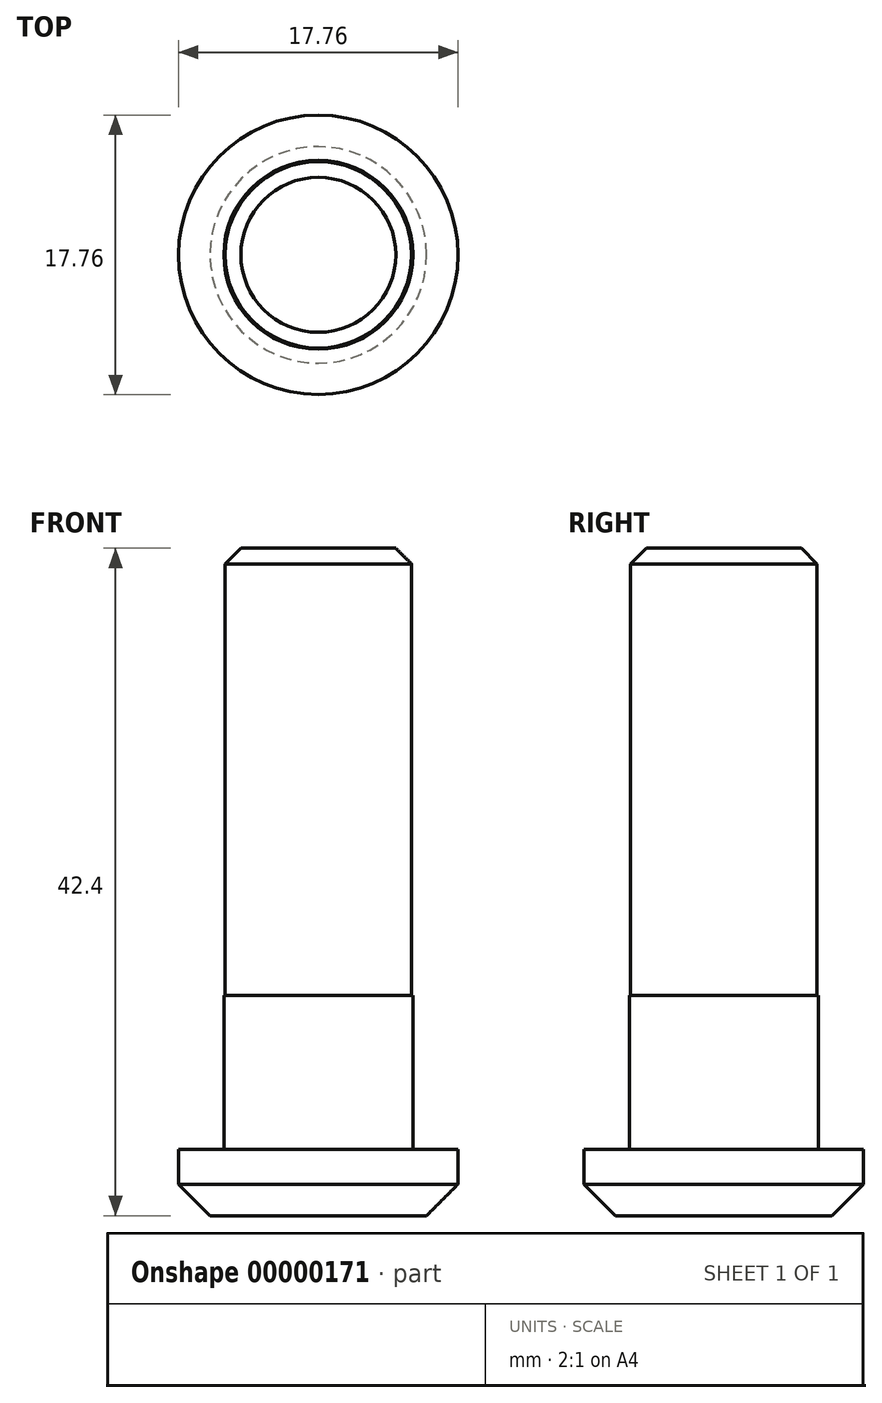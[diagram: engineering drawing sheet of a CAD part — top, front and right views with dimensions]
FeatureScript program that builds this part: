
annotation { "Feature Type Name" : "Feature", "Feature Type Description" : "" }
export const myFeature = defineFeature(function(context is Context, id is Id, definition is map)
    precondition{}
    {
        {
            var Q0;
            Q0=qCreatedBy(makeId("Top.planeOp"),FACE);
            var sketch = newSketch(context, id + "F0", { "sketchPlane" : qUnion([Q0])});
            skCircle(sketch, "E0", {"center": v(0, 0) * mm, "radius": 8.88 * mm});
            skSolve(sketch);
        }
        {
            var Q0;
            Q0=makeQuery(id+"F0.imprint","IMPRINT",FACE,{"disambiguationData":[TD([[makeQuery(id+"F0.imprint","IMPRINT",EDGE,{"derivedFrom":sQuery(id+"F0.wireOp",EDGE,"E0")}),1.0]])]});
            extrude(context, id + "F1", {"entities" : qUnion([Q0]), "depth" : 4.2 * mm});
        }
        {
            var Q0;
            Q0=qCreatedBy(makeId("Top.planeOp"),FACE);
            var sketch = newSketch(context, id + "F2", { "sketchPlane" : qUnion([Q0])});
            skCircle(sketch, "E1", {"center": v(0, 0) * mm, "radius": 6 * mm});
            skSolve(sketch);
        }
        {
            var Q0;
            Q0=makeQuery(id+"F2.imprint","IMPRINT",FACE,{"disambiguationData":[TD([[makeQuery(id+"F2.imprint","IMPRINT",EDGE,{"derivedFrom":sQuery(id+"F2.wireOp",EDGE,"E1")}),1.0]])]});
            extrude(context, id + "F3", {"entities" : qUnion([Q0]), "operationType" : NewBodyOperationType.ADD, "depth" : 14 * mm});
        }
        {
            var Q0;
            Q0=qCreatedBy(makeId("Top.planeOp"),FACE);
            var sketch = newSketch(context, id + "F4", { "sketchPlane" : qUnion([Q0])});
            skCircle(sketch, "E2", {"center": v(0, 0) * mm, "radius": 5.92 * mm});
            skSolve(sketch);
        }
        {
            var Q0;
            Q0=makeQuery(id+"F4.imprint","IMPRINT",FACE,{"disambiguationData":[TD([[makeQuery(id+"F4.imprint","IMPRINT",EDGE,{"derivedFrom":sQuery(id+"F4.wireOp",EDGE,"E2")}),1.0]])]});
            extrude(context, id + "F5", {"entities" : qUnion([Q0]), "operationType" : NewBodyOperationType.ADD, "depth" : 42.4 * mm});
        }
        {
            var Q0;
            Q0=makeQuery(id+"F5.opExtrude","CAP_EDGE",EDGE,{"disambiguationData":[OSD([sQuery(id+"F4.wireOp",EDGE,"E2")])],"isStart":false});
            chamfer(context, id + "F6", {"entities" : qUnion([Q0]), "width" : 1 * mm, "tangentPropagation" : true});
        }
        {
            var Q0;
            Q0=makeQuery(id+"F1.opExtrude","CAP_EDGE",EDGE,{"disambiguationData":[OSD([sQuery(id+"F0.wireOp",EDGE,"E0")])],"isStart":true});
            chamfer(context, id + "F7", {"entities" : qUnion([Q0]), "width" : 2 * mm, "tangentPropagation" : true});
        }
    });
